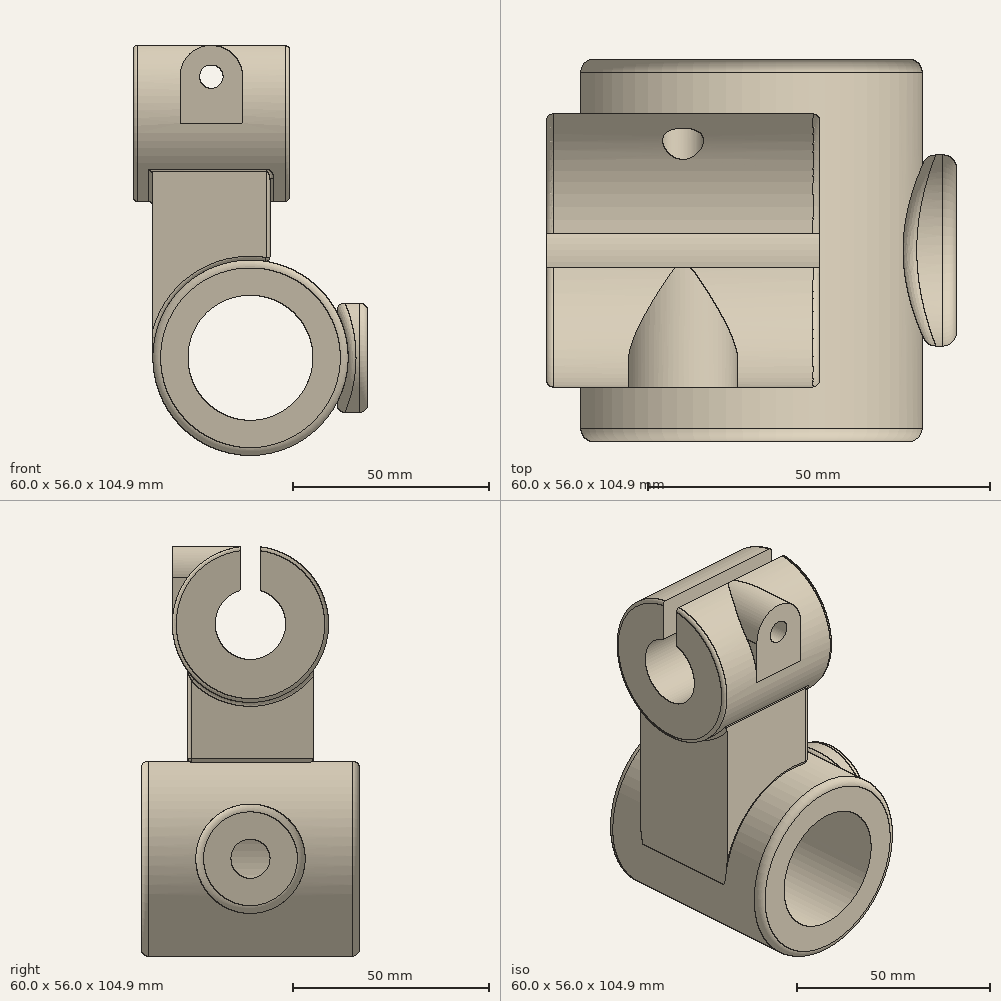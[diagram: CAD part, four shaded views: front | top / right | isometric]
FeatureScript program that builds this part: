
annotation { "Feature Type Name" : "Feature", "Feature Type Description" : "" }
export const myFeature = defineFeature(function(context is Context, id is Id, definition is map)
    precondition{}
    {
        {
            var Q0;
            Q0=qCreatedBy(makeId("Front.planeOp"),FACE);
            var sketch = newSketch(context, id + "F0", { "sketchPlane" : qUnion([Q0])});
            skCircle(sketch, "E0", {"center": v(0, 0) * mm, "radius": 25 * mm});
            skCircle(sketch, "E1", {"center": v(0, 0) * mm, "radius": 16 * mm});
            skSolve(sketch);
        }
        {
            var Q0;
            Q0 = qSketchRegion(id + "F0", true);
            extrude(context, id + "F1", {"entities" : qUnion([Q0]), "depth" : 56 * mm, "symmetric" : true});
        }
        {
            var Q0;
            Q0=qCreatedBy(makeId("Right.planeOp"),FACE);
            cPlane(context, id + "F2", {"entities" : qUnion([Q0]), "cplaneType" : CPlaneType.OFFSET, "offset" : 30 * mm, "width" : 150 * mm, "height" : 150 * mm});
        }
        {
            var Q0;
            Q0=qCreatedBy(id+"F2.planeOp",FACE);
            var sketch = newSketch(context, id + "F3", { "sketchPlane" : qUnion([Q0])});
            skCircle(sketch, "E2", {"center": v(0, 0) * mm, "radius": 14 * mm});
            skSolve(sketch);
        }
        {
            var Q0;
            Q0 = qSketchRegion(id + "F3", true);
            extrude(context, id + "F4", {"entities" : qUnion([Q0]), "endBound" : BoundingType.UP_TO_NEXT, "oppositeDirection" : true, "depth" : 25 * mm});
        }
        {
            var Q0;
            Q0=makeQuery(id+"F4.opExtrude","CAP_FACE",FACE,{"disambiguationData":[OSD([sQuery(id+"F3.wireOp",EDGE,"E2")])],"isStart":true});
            var sketch = newSketch(context, id + "F5", { "sketchPlane" : qUnion([Q0])});
            skCircle(sketch, "E3", {"center": v(0, 0) * mm, "radius": 5 * mm});
            skSolve(sketch);
        }
        {
            var Q0;
            Q0 = qSketchRegion(id + "F5", true);
            extrude(context, id + "F6", {"entities" : qUnion([Q0]), "operationType" : NewBodyOperationType.REMOVE, "oppositeDirection" : true, "depth" : 30 * mm});
        }
        {
            var Q0;
            Q0=qCreatedBy(makeId("Right.planeOp"),FACE);
            cPlane(context, id + "F7", {"entities" : qUnion([Q0]), "cplaneType" : CPlaneType.OFFSET, "offset" : 10 * mm, "oppositeDirection" : true, "width" : 150 * mm, "height" : 150 * mm});
        }
        {
            var Q0;
            Q0=qCreatedBy(id+"F7.planeOp",FACE);
            var sketch = newSketch(context, id + "F8", { "sketchPlane" : qUnion([Q0])});
            skCircle(sketch, "E4", {"center": v(0, 60) * mm, "radius": 20 * mm});
            skSolve(sketch);
        }
        {
            var Q0;
            Q0=makeQuery(id+"F8.imprint","IMPRINT",FACE,{"disambiguationData":[TD([[makeQuery(id+"F8.imprint","IMPRINT",EDGE,{"derivedFrom":sQuery(id+"F8.wireOp",EDGE,"E4")}),1.0]])]});
            extrude(context, id + "F9", {"entities" : qUnion([Q0]), "depth" : 40 * mm, "symmetric" : true});
        }
        {
            var Q0;
            Q0=makeQuery(id+"F9.opExtrude","CAP_FACE",FACE,{"disambiguationData":[OSD([sQuery(id+"F8.wireOp",EDGE,"E4")])],"isStart":false});
            var sketch = newSketch(context, id + "F10", { "sketchPlane" : qUnion([Q0])});
            skArc(sketch, "E5", {"start": v(-2.5, 68.65) * mm, "mid": v(0, 51) * mm, "end": v(2.5, 68.65) * mm});
            skLineSegment(sketch, "E6", {"start": v(2.5, 68.65) * mm, "end": v(2.5, 87.04) * mm});
            skLineSegment(sketch, "E7", {"start": v(-2.5, 68.65) * mm, "end": v(-2.5, 89.85) * mm});
            skLineSegment(sketch, "E8", {"start": v(2.5, 87.04) * mm, "end": v(-2.5, 89.85) * mm});
            skSolve(sketch);
        }
        {
            var Q0;
            Q0 = qSketchRegion(id + "F10", true);
            extrude(context, id + "F11", {"entities" : qUnion([Q0]), "operationType" : NewBodyOperationType.REMOVE, "endBound" : BoundingType.THROUGH_ALL, "oppositeDirection" : true, "depth" : 25 * mm});
        }
        {
            var Q0;
            Q0=qCreatedBy(makeId("Front.planeOp"),FACE);
            var sketch = newSketch(context, id + "F12", { "sketchPlane" : qUnion([Q0])});
            skArc(sketch, "E9.0", {"start": v(5, 24.5) * mm, "mid": v(-15.81, 19.36) * mm, "end": v(-25, 0) * mm});
            skLineSegment(sketch, "E10", {"start": v(5, 41.64) * mm, "end": v(5, 24.5) * mm});
            skLineSegment(sketch, "E11", {"start": v(-25, 0) * mm, "end": v(-25, 41.33) * mm});
            skPoint(sketch, "E12.end.orphan", {"position": v(5, 43.28) * mm});
            skPoint(sketch, "E13.start.orphan", {"position": v(-25, 45.83) * mm});
            skPoint(sketch, "E14.start.orphan", {"position": v(-25, 43.28) * mm});
            skLineSegment(sketch, "E15", {"start": v(5, 41.64) * mm, "end": v(5, 50.54) * mm});
            skLineSegment(sketch, "E16", {"start": v(5, 50.54) * mm, "end": v(-25, 50.54) * mm});
            skLineSegment(sketch, "E17", {"start": v(-25, 50.54) * mm, "end": v(-25, 41.33) * mm});
            skSolve(sketch);
        }
        {
            var Q0;
            Q0 = qSketchRegion(id + "F12", true);
            extrude(context, id + "F13", {"entities" : qUnion([Q0]), "depth" : 32 * mm, "symmetric" : true});
        }
        {
            var Q0;
            Q0=makeQuery(id+"F4.opExtrude","CAP_EDGE",EDGE,{"disambiguationData":[OSD([sQuery(id+"F3.wireOp",EDGE,"E2")])],"isStart":false});
            fillet(context, id + "F14", {"entities" : qUnion([Q0]), "radius" : 2 * mm, "tangentPropagation" : true, "allowEdgeOverflow" : false});
        }
        {
            var Q0;
            Q0=makeQuery(id+"F4.opExtrude","CAP_EDGE",EDGE,{"disambiguationData":[OSD([sQuery(id+"F3.wireOp",EDGE,"E2")])],"isStart":true});
            fillet(context, id + "F15", {"entities" : qUnion([Q0]), "radius" : 2 * mm, "tangentPropagation" : true, "allowEdgeOverflow" : false});
        }
        {
            var Q0;
            Q0=makeQuery(id+"F1.opExtrude","CAP_EDGE",EDGE,{"disambiguationData":[OSD([sQuery(id+"F0.wireOp",EDGE,"E0")])],"isStart":true});
            fillet(context, id + "F16", {"entities" : qUnion([Q0]), "radius" : 2 * mm, "tangentPropagation" : true, "allowEdgeOverflow" : false});
        }
        {
            var Q0;
            Q0=makeQuery(id+"F1.opExtrude","CAP_EDGE",EDGE,{"disambiguationData":[OSD([sQuery(id+"F0.wireOp",EDGE,"E0")])],"isStart":false});
            fillet(context, id + "F17", {"entities" : qUnion([Q0]), "radius" : 2 * mm, "tangentPropagation" : true, "allowEdgeOverflow" : false});
        }
        {
            var Q0;
            Q0=makeQuery(id+"F4.opExtrude","SWEPT_BODY",BODY,{"disambiguationData":[OSD([sQuery(id+"F3.wireOp",EDGE,"E2")])]});
            var Q1;
            Q1=makeQuery(id+"F13.opExtrude","SWEPT_BODY",BODY,{"disambiguationData":[OSD([sQuery(id+"F12.wireOp",EDGE,"E9.0"),sQuery(id+"F12.wireOp",EDGE,"E10"),sQuery(id+"F12.wireOp",EDGE,"E11"),sQuery(id+"F12.wireOp",EDGE,"E15"),sQuery(id+"F12.wireOp",EDGE,"E16"),sQuery(id+"F12.wireOp",EDGE,"E17")])]});
            var Q2;
            Q2=makeQuery(id+"F9.opExtrude","SWEPT_BODY",BODY,{"disambiguationData":[OSD([sQuery(id+"F8.wireOp",EDGE,"E4")])]});
            booleanBodies(context, id + "F18", {"operationType" : BooleanOperationType.UNION, "tools" : qUnion([Q0, Q1, Q2])});
        }
        {
            var Q0;
            Q0=makeQuery(id+"F13.opExtrude","CAP_EDGE",EDGE,{"disambiguationData":[OSD([sQuery(id+"F12.wireOp",EDGE,"E9.0")])],"isStart":false});
            fillet(context, id + "F19", {"entities" : qUnion([Q0]), "radius" : 1 * mm, "tangentPropagation" : true, "allowEdgeOverflow" : false});
        }
        {
            var Q0;
            Q0=makeQuery(id+"F13.opExtrude","SWEPT_EDGE",EDGE,{"disambiguationData":[OSD([sQuery(id+"F12.wireOp",EDGE,"E9.0"),sQuery(id+"F12.wireOp",EDGE,"E10")])]});
            var Q1;
            Q1=makeQuery(id+"F13.opExtrude","CAP_EDGE",EDGE,{"disambiguationData":[OSD([sQuery(id+"F12.wireOp",EDGE,"E9.0")])],"isStart":true});
            fillet(context, id + "F20", {"entities" : qUnion([Q0, Q1]), "radius" : 1 * mm, "tangentPropagation" : true, "allowEdgeOverflow" : false});
        }
        {
            var Q0;
            Q0=makeQuery(id+"F18.opBoolean","INTERSECT",EDGE,{"derivedFrom":[makeQuery(id+"F9.opExtrude","SWEPT_FACE",FACE,{"disambiguationData":[OSD([sQuery(id+"F8.wireOp",EDGE,"E4")])]}),makeQuery(id+"F13.opExtrude","CAP_FACE",FACE,{"disambiguationData":[OSD([sQuery(id+"F12.wireOp",EDGE,"E9.0"),sQuery(id+"F12.wireOp",EDGE,"E10"),sQuery(id+"F12.wireOp",EDGE,"E11"),sQuery(id+"F12.wireOp",EDGE,"E15"),sQuery(id+"F12.wireOp",EDGE,"E16"),sQuery(id+"F12.wireOp",EDGE,"E17")])],"isStart":true})]});
            var Q1;
            Q1=makeQuery(id+"F18.opBoolean","INTERSECT",EDGE,{"derivedFrom":[makeQuery(id+"F9.opExtrude","SWEPT_FACE",FACE,{"disambiguationData":[OSD([sQuery(id+"F8.wireOp",EDGE,"E4")])]}),makeQuery(id+"F13.opExtrude","SWEPT_FACE",FACE,{"disambiguationData":[OSD([sQuery(id+"F12.wireOp",EDGE,"E11"),sQuery(id+"F12.wireOp",EDGE,"E17")])]})]});
            var Q2;
            Q2=makeQuery(id+"F18.opBoolean","INTERSECT",EDGE,{"derivedFrom":[makeQuery(id+"F9.opExtrude","SWEPT_FACE",FACE,{"disambiguationData":[OSD([sQuery(id+"F8.wireOp",EDGE,"E4")])]}),makeQuery(id+"F13.opExtrude","CAP_FACE",FACE,{"disambiguationData":[OSD([sQuery(id+"F12.wireOp",EDGE,"E9.0"),sQuery(id+"F12.wireOp",EDGE,"E10"),sQuery(id+"F12.wireOp",EDGE,"E11"),sQuery(id+"F12.wireOp",EDGE,"E15"),sQuery(id+"F12.wireOp",EDGE,"E16"),sQuery(id+"F12.wireOp",EDGE,"E17")])],"isStart":false})]});
            var Q3;
            Q3=makeQuery(id+"F18.opBoolean","INTERSECT",EDGE,{"derivedFrom":[makeQuery(id+"F9.opExtrude","SWEPT_FACE",FACE,{"disambiguationData":[OSD([sQuery(id+"F8.wireOp",EDGE,"E4")])]}),makeQuery(id+"F13.opExtrude","SWEPT_FACE",FACE,{"disambiguationData":[OSD([sQuery(id+"F12.wireOp",EDGE,"E10"),sQuery(id+"F12.wireOp",EDGE,"E15")])]})]});
            fillet(context, id + "F21", {"entities" : qUnion([Q0, Q1, Q2, Q3]), "radius" : 1 * mm, "tangentPropagation" : true, "allowEdgeOverflow" : false});
        }
        {
            var Q0;
            Q0=makeQuery(id+"F9.opExtrude","CAP_EDGE",EDGE,{"disambiguationData":[OSD([sQuery(id+"F8.wireOp",EDGE,"E4")])],"isStart":false});
            var Q1;
            Q1=makeQuery(id+"F9.opExtrude","CAP_EDGE",EDGE,{"disambiguationData":[OSD([sQuery(id+"F8.wireOp",EDGE,"E4")])],"isStart":true});
            fillet(context, id + "F22", {"entities" : qUnion([Q0, Q1]), "radius" : 1 * mm, "tangentPropagation" : true, "allowEdgeOverflow" : false});
        }
        {
            var Q0;
            Q0=qCreatedBy(makeId("Front.planeOp"),FACE);
            cPlane(context, id + "F23", {"entities" : qUnion([Q0]), "cplaneType" : CPlaneType.OFFSET, "offset" : 20 * mm, "width" : 150 * mm, "height" : 150 * mm});
        }
        {
            var Q0;
            Q0=qCreatedBy(id+"F23.planeOp",FACE);
            var sketch = newSketch(context, id + "F24", { "sketchPlane" : qUnion([Q0])});
            skLineSegment(sketch, "E18", {"start": v(-2, 59.92) * mm, "end": v(-17.99, 59.92) * mm});
            skLineSegment(sketch, "E19", {"start": v(-10, 59.92) * mm, "end": v(-10, 82.2) * mm});
            skArc(sketch, "E20", {"start": v(-2, 71.88) * mm, "mid": v(-10.22, 79.91) * mm, "end": v(-17.99, 71.44) * mm});
            skLineSegment(sketch, "E21", {"start": v(-17.99, 71.44) * mm, "end": v(-17.99, 59.92) * mm});
            skLineSegment(sketch, "E22", {"start": v(-2, 71.96) * mm, "end": v(-2, 59.92) * mm});
            skPoint(sketch, "E23.0.end.orphan", {"position": v(-30, 41) * mm});
            skPoint(sketch, "E24.0.end.orphan", {"position": v(10, 41) * mm});
            skSolve(sketch);
        }
        {
            var Q0;
            Q0 = qSketchRegion(id + "F24", true);
            extrude(context, id + "F25", {"entities" : qUnion([Q0]), "operationType" : NewBodyOperationType.ADD, "oppositeDirection" : true, "depth" : 17.5 * mm});
        }
        {
            var Q0;
            Q0=makeQuery(id+"F4.opExtrude","SWEPT_BODY",BODY,{"disambiguationData":[OSD([sQuery(id+"F3.wireOp",EDGE,"E2")])]});
            var Q1;
            Q1=qCreatedBy(makeId("Front.planeOp"),FACE);
            mirror(context, id + "F26", {"operationType" : NewBodyOperationType.ADD, "entities" : qUnion([Q0]), "mirrorPlane" : qUnion([Q1])});
        }
        {
            var Q0;
            Q0=makeQuery(id+"F9.opExtrude","CAP_FACE",FACE,{"disambiguationData":[OSD([sQuery(id+"F8.wireOp",EDGE,"E4")])],"isStart":false});
            var sketch = newSketch(context, id + "F27", { "sketchPlane" : qUnion([Q0])});
            skArc(sketch, "E25.0", {"start": v(-2.5, 68.65) * mm, "mid": v(0, 51) * mm, "end": v(2.5, 68.65) * mm});
            skLineSegment(sketch, "E26", {"start": v(-2.5, 68.65) * mm, "end": v(2.5, 68.65) * mm});
            skSolve(sketch);
        }
        {
            var Q0;
            Q0 = qSketchRegion(id + "F27", true);
            extrude(context, id + "F28", {"entities" : qUnion([Q0]), "operationType" : NewBodyOperationType.REMOVE, "endBound" : BoundingType.THROUGH_ALL, "oppositeDirection" : true, "depth" : 25 * mm});
        }
        {
            var Q0;
            Q0=makeQuery(id+"F25.opExtrude","CAP_FACE",FACE,{"disambiguationData":[OSD([sQuery(id+"F24.wireOp",EDGE,"E18"),sQuery(id+"F24.wireOp",EDGE,"E20"),sQuery(id+"F24.wireOp",EDGE,"E21"),sQuery(id+"F24.wireOp",EDGE,"E22")])],"isStart":true});
            var sketch = newSketch(context, id + "F29", { "sketchPlane" : qUnion([Q0])});
            skCircle(sketch, "E27", {"center": v(-10, 71.92) * mm, "radius": 3 * mm});
            skSolve(sketch);
        }
        {
            var Q0;
            Q0 = qSketchRegion(id + "F29", true);
            extrude(context, id + "F30", {"entities" : qUnion([Q0]), "operationType" : NewBodyOperationType.REMOVE, "endBound" : BoundingType.THROUGH_ALL, "oppositeDirection" : true, "depth" : 25 * mm});
        }
    });
